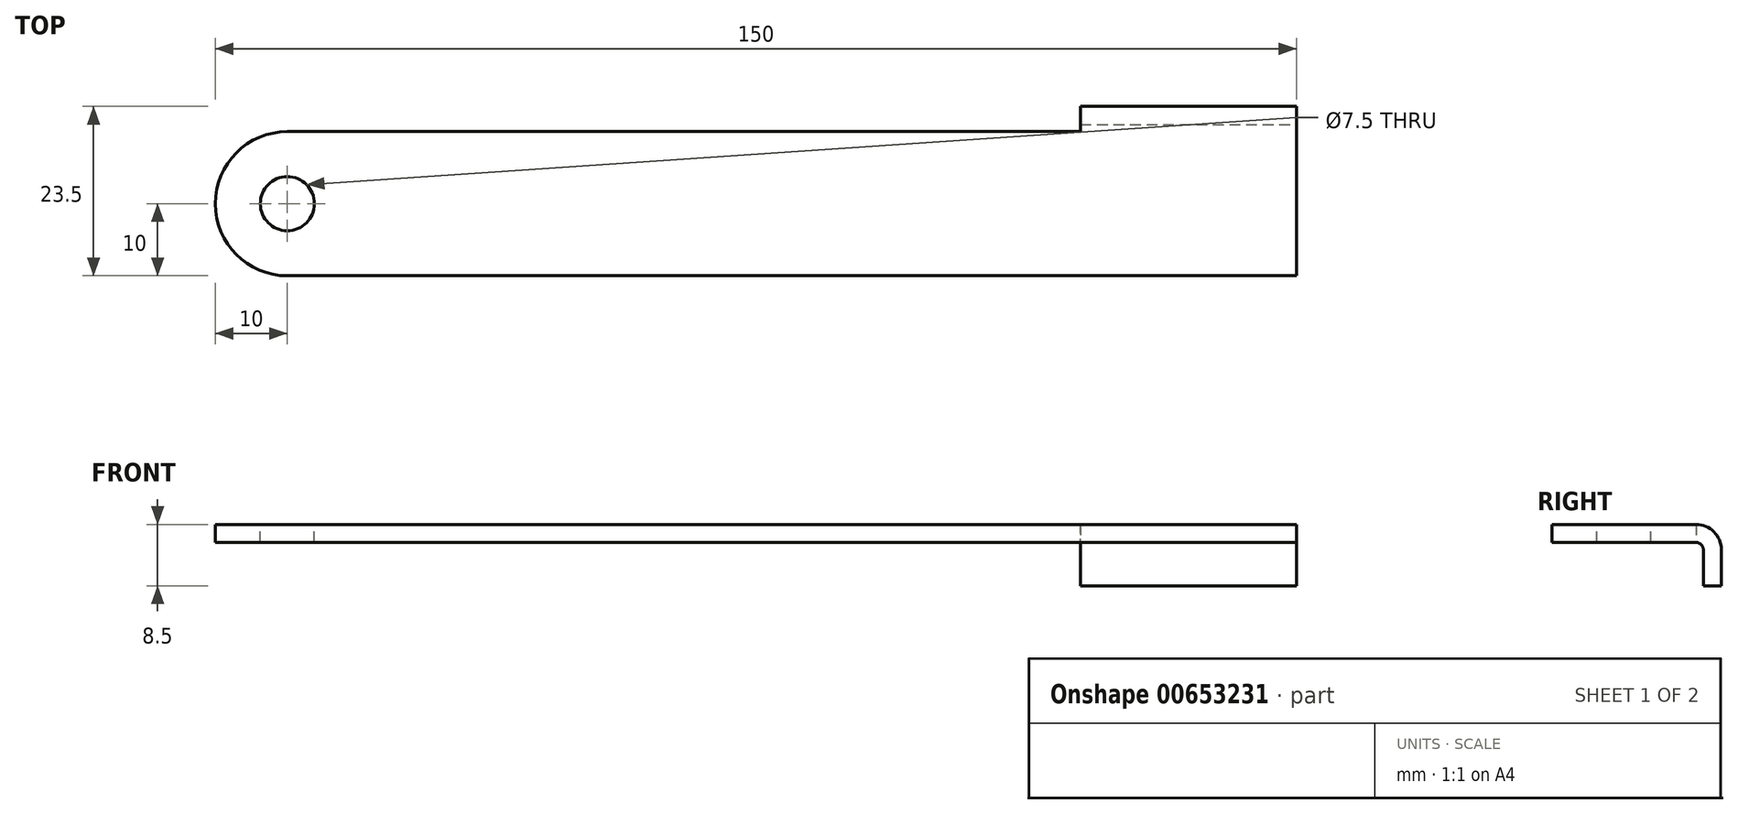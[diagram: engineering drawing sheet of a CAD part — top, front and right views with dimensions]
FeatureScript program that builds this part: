
annotation { "Feature Type Name" : "Feature", "Feature Type Description" : "" }
export const myFeature = defineFeature(function(context is Context, id is Id, definition is map)
    precondition{}
    {
        {
            var Q0;
            Q0=qCreatedBy(makeId("Top.planeOp"),FACE);
            var sketch = newSketch(context, id + "F0", { "sketchPlane" : qUnion([Q0])});
            skLineSegment(sketch, "E0.bottom", {"start": v(75, 10) * mm, "end": v(-75, 10) * mm});
            skLineSegment(sketch, "E0.top", {"start": v(75, -10) * mm, "end": v(-75, -10) * mm});
            skLineSegment(sketch, "E0.left", {"start": v(75, 10) * mm, "end": v(75, -10) * mm});
            skLineSegment(sketch, "E0.right", {"start": v(-75, 10) * mm, "end": v(-75, -10) * mm});
            skPoint(sketch, "E0.middle", {"position": v(0, 0) * mm});
            skSolve(sketch);
        }
        {
            var Q0;
            Q0=qSketchRegion(id+"F0",true);
            extrude(context, id + "F1", {"entities" : qUnion([Q0]), "depth" : 2.5 * mm, "offsetDistance" : 25 * mm});
        }
        {
            var Q0;
            Q0=makeQuery(id+"F1.opExtrude","CAP_FACE",FACE,{"disambiguationData":[OSD([sQuery(id+"F0.wireOp",EDGE,"E0.bottom"),sQuery(id+"F0.wireOp",EDGE,"E0.top"),sQuery(id+"F0.wireOp",EDGE,"E0.left"),sQuery(id+"F0.wireOp",EDGE,"E0.right")])],"isStart":false});
            var sketch = newSketch(context, id + "F2", { "sketchPlane" : qUnion([Q0])});
            skPoint(sketch, "E1", {"position": v(-65, 0) * mm});
            skPoint(sketch, "E1.positionSnap0", {"position": v(-75, 0) * mm});
            skSolve(sketch);
        }
        {
            var Q0;
            Q0=sQuery(id+"F2.wireOp",VERTEX,"E1");
            var Q1;
            Q1=makeQuery(id+"F1.opExtrude","SWEPT_BODY",BODY,{"disambiguationData":[OSD([sQuery(id+"F0.wireOp",EDGE,"E0.bottom"),sQuery(id+"F0.wireOp",EDGE,"E0.top"),sQuery(id+"F0.wireOp",EDGE,"E0.left"),sQuery(id+"F0.wireOp",EDGE,"E0.right")])]});
            hole(context, id + "F3", {"style" : HoleStyle.SIMPLE, "endStyle" : HoleEndStyle.THROUGH, "holeDiameter" : 7.5 * mm, "majorDiameter" : 4 * mm, "isTappedThrough" : true, "tappedDepth" : 12 * mm, "tapClearance" : 3, "startFromSketch" : true, "locations" : qUnion([Q0]), "scope" : qUnion([Q1])});
        }
        {
            var Q0;
            Q0=makeQuery(id+"F1.opExtrude","SWEPT_EDGE",EDGE,{"disambiguationData":[OSD([sQuery(id+"F0.wireOp",EDGE,"E0.top"),sQuery(id+"F0.wireOp",EDGE,"E0.right")])]});
            var Q1;
            Q1=makeQuery(id+"F1.opExtrude","SWEPT_EDGE",EDGE,{"disambiguationData":[OSD([sQuery(id+"F0.wireOp",EDGE,"E0.bottom"),sQuery(id+"F0.wireOp",EDGE,"E0.right")])]});
            fillet(context, id + "F4", {"entities" : qUnion([Q0, Q1]), "radius" : 10 * mm, "tangentPropagation" : true, "allowEdgeOverflow" : false});
        }
        {
            var Q0;
            Q0=makeQuery(id+"F1.opExtrude","SWEPT_FACE",FACE,{"disambiguationData":[OSD([sQuery(id+"F0.wireOp",EDGE,"E0.left")])]});
            var sketch = newSketch(context, id + "F5", { "sketchPlane" : qUnion([Q0])});
            skLineSegment(sketch, "E2.0", {"start": v(10, 2.5) * mm, "end": v(-10, 2.5) * mm, "construction": true});
            skLineSegment(sketch, "E3.0", {"start": v(10, 0) * mm, "end": v(-10, 0) * mm, "construction": true});
            skLineSegment(sketch, "E4.bottom", {"start": v(11, -6) * mm, "end": v(13.5, -6) * mm});
            skLineSegment(sketch, "E4.top", {"start": v(11, -1) * mm, "end": v(13.5, -1) * mm});
            skLineSegment(sketch, "E4.left", {"start": v(11, -6) * mm, "end": v(11, -1) * mm});
            skLineSegment(sketch, "E4.right", {"start": v(13.5, -6) * mm, "end": v(13.5, -1) * mm});
            skArc(sketch, "E5", {"start": v(10, 2.5) * mm, "mid": v(12.47, 1.47) * mm, "end": v(13.5, -1) * mm});
            skArc(sketch, "E6", {"start": v(10, 0) * mm, "mid": v(10.7, -0.3) * mm, "end": v(11, -1) * mm});
            skSolve(sketch);
        }
        {
            var Q0;
            Q0=makeQuery(id+"F5.imprint","IMPRINT",FACE,{"disambiguationData":[TD([[makeQuery(id+"F5.imprint","IMPRINT",EDGE,{"derivedFrom":sQuery(id+"F5.wireOp",EDGE,"E4.top")}),1.0]])]});
            var Q1;
            Q1=makeQuery(id+"F5.imprint","IMPRINT",FACE,{"disambiguationData":[TD([[makeQuery(id+"F5.imprint","IMPRINT",EDGE,{"derivedFrom":sQuery(id+"F5.wireOp",EDGE,"E4.bottom")}),1.0]])]});
            extrude(context, id + "F6", {"entities" : qUnion([Q0, Q1]), "operationType" : NewBodyOperationType.ADD, "oppositeDirection" : true, "depth" : 30 * mm, "offsetDistance" : 25 * mm});
        }
    });
